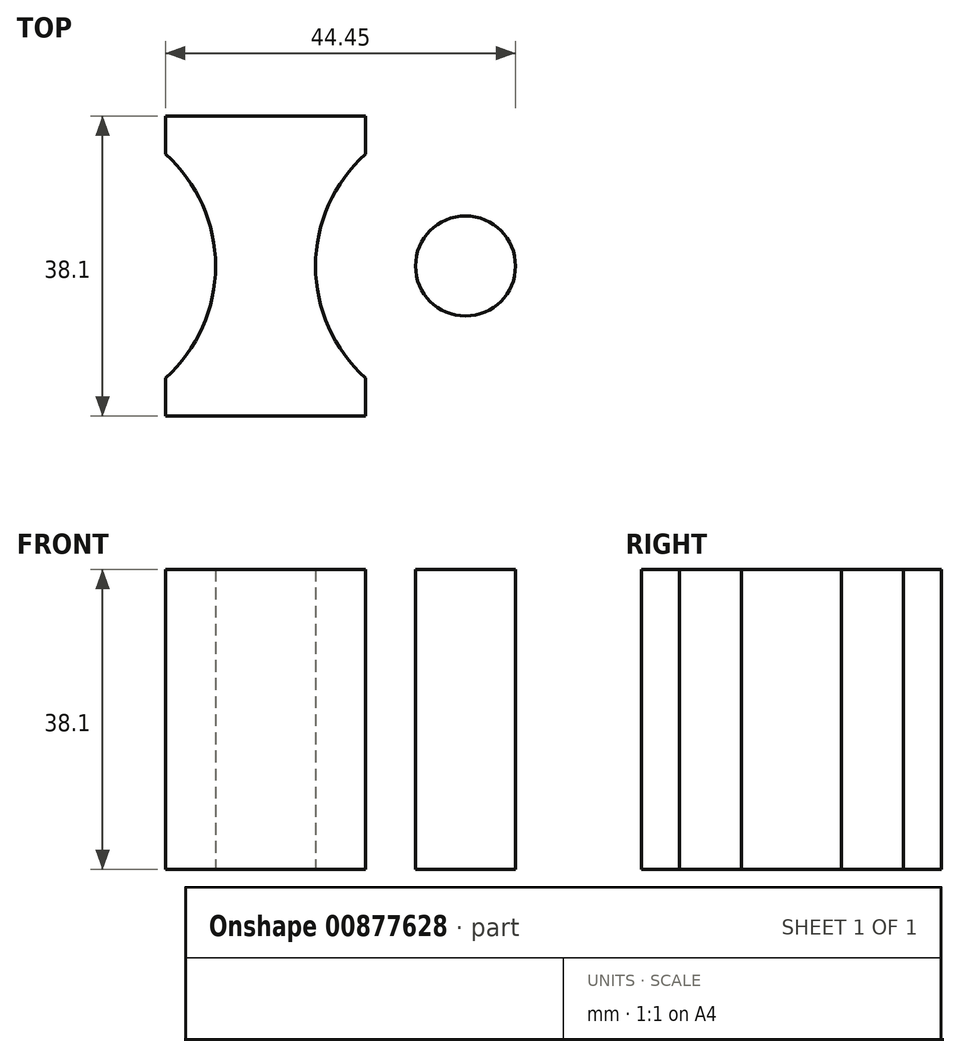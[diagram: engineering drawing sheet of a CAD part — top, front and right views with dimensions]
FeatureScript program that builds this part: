
annotation { "Feature Type Name" : "Feature", "Feature Type Description" : "" }
export const myFeature = defineFeature(function(context is Context, id is Id, definition is map)
    precondition{}
    {
        {
            var Q0;
            Q0=qCreatedBy(makeId("Top.planeOp"),FACE);
            var sketch = newSketch(context, id + "F0", { "sketchPlane" : qUnion([Q0])});
            skCircle(sketch, "E0", {"center": v(-25.4, 0) * mm, "radius": 6.35 * mm});
            skArc(sketch, "E1", {"start": v(-38.1, 14.2) * mm, "mid": v(-44.45, 0) * mm, "end": v(-38.1, -14.2) * mm});
            skLineSegment(sketch, "E2", {"start": v(-50.8, 43.98) * mm, "end": v(-50.8, -43.63) * mm, "construction": true});
            skArc(sketch, "E3.MirrorCS", {"start": v(-63.5, 14.2) * mm, "mid": v(-57.15, 0) * mm, "end": v(-63.5, -14.2) * mm});
            skCircle(sketch, "E4.MirrorC", {"center": v(-76.2, 0) * mm, "radius": 6.35 * mm});
            skLineSegment(sketch, "E5", {"start": v(-25.4, 55.98) * mm, "end": v(-25.4, -42.73) * mm, "construction": true});
            skPoint(sketch, "E6.MirrorCS.end.orphan", {"position": v(-63.5, 14.2) * mm});
            skPoint(sketch, "E7.MirrorCS.start.orphan", {"position": v(-63.5, -14.2) * mm});
            skLineSegment(sketch, "E8", {"start": v(-63.5, 19.05) * mm, "end": v(-63.5, 14.2) * mm});
            skLineSegment(sketch, "E9", {"start": v(-38.1, 19.05) * mm, "end": v(-38.1, 14.2) * mm});
            skLineSegment(sketch, "E10", {"start": v(-38.1, -14.2) * mm, "end": v(-38.1, -19.05) * mm});
            skLineSegment(sketch, "E11", {"start": v(-63.5, -14.2) * mm, "end": v(-63.5, -19.05) * mm});
            skLineSegment(sketch, "E12", {"start": v(-38.1, 19.05) * mm, "end": v(-63.5, 19.05) * mm});
            skLineSegment(sketch, "E13", {"start": v(-38.1, -19.05) * mm, "end": v(-63.5, -19.05) * mm});
            skSolve(sketch);
        }
        {
            var Q0;
            Q0=makeQuery(id+"F0.imprint","IMPRINT",FACE,{"disambiguationData":[TD([[makeQuery(id+"F0.imprint","IMPRINT",EDGE,{"derivedFrom":sQuery(id+"F0.wireOp",EDGE,"E4.MirrorC")}),-1.0]])]});
            var Q1;
            Q1=makeQuery(id+"F0.imprint","IMPRINT",FACE,{"disambiguationData":[TD([[makeQuery(id+"F0.imprint","IMPRINT",EDGE,{"derivedFrom":sQuery(id+"F0.wireOp",EDGE,"E1")}),-1.0]])]});
            var Q2;
            Q2=makeQuery(id+"F0.imprint","IMPRINT",FACE,{"disambiguationData":[TD([[makeQuery(id+"F0.imprint","IMPRINT",EDGE,{"derivedFrom":sQuery(id+"F0.wireOp",EDGE,"E0")}),1.0]])]});
            extrude(context, id + "F1", {"entities" : qUnion([Q0, Q1, Q2]), "depth" : 38.1 * mm, "offsetDistance" : 25.4 * mm});
        }
    });
